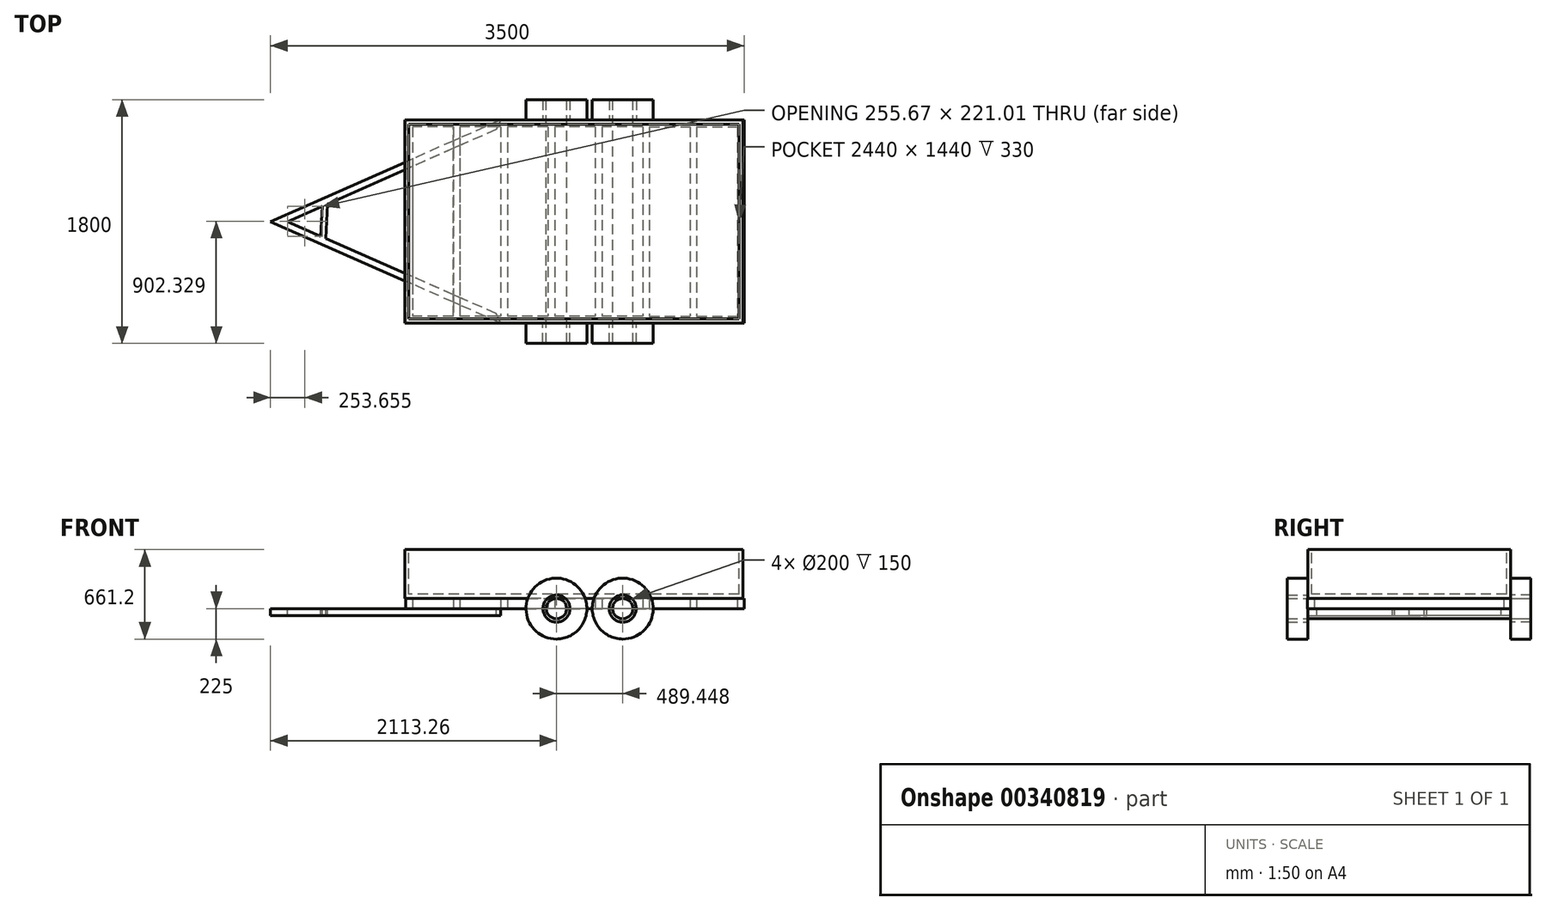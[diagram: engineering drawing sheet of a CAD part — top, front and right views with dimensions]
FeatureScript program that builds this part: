
annotation { "Feature Type Name" : "Feature", "Feature Type Description" : "" }
export const myFeature = defineFeature(function(context is Context, id is Id, definition is map)
    precondition{}
    {
        {
            var Q0;
            Q0=qCreatedBy(makeId("Top.planeOp"),FACE);
            var sketch = newSketch(context, id + "F0", { "sketchPlane" : qUnion([Q0])});
            skLineSegment(sketch, "E0.bottom", {"start": v(1069.78, 749.77) * mm, "end": v(-1430.22, 749.77) * mm});
            skLineSegment(sketch, "E0.top", {"start": v(1069.78, -750.23) * mm, "end": v(-1430.22, -750.23) * mm});
            skLineSegment(sketch, "E0.left", {"start": v(1069.78, 749.77) * mm, "end": v(1069.78, -750.23) * mm});
            skLineSegment(sketch, "E0.right", {"start": v(-1430.22, 749.77) * mm, "end": v(-1430.22, -750.23) * mm});
            skLineSegment(sketch, "E1.0", {"start": v(-1380.22, 699.77) * mm, "end": v(-1380.22, -700.23) * mm});
            skLineSegment(sketch, "E2.left", {"start": v(-1080.22, 699.77) * mm, "end": v(-1080.22, -700.23) * mm});
            skLineSegment(sketch, "E3.trimOffspring", {"start": v(-1080.22, 699.77) * mm, "end": v(-1380.22, 699.77) * mm});
            skLineSegment(sketch, "E4.trimOffspring", {"start": v(-1080.22, -700.23) * mm, "end": v(-1380.22, -700.23) * mm});
            skLineSegment(sketch, "E5.1.0.0", {"start": v(-730.22, 699.77) * mm, "end": v(-730.22, -700.23) * mm});
            skLineSegment(sketch, "E5.1.0.1", {"start": v(-730.22, 699.77) * mm, "end": v(-1030.22, 699.77) * mm});
            skLineSegment(sketch, "E5.1.0.2", {"start": v(-1030.22, 699.77) * mm, "end": v(-1030.22, -700.23) * mm});
            skLineSegment(sketch, "E5.1.0.3", {"start": v(-730.22, -700.23) * mm, "end": v(-1030.22, -700.23) * mm});
            skLineSegment(sketch, "E5.2.0.0", {"start": v(-380.22, 699.77) * mm, "end": v(-380.22, -700.23) * mm});
            skLineSegment(sketch, "E5.2.0.1", {"start": v(-380.22, 699.77) * mm, "end": v(-680.22, 699.77) * mm});
            skLineSegment(sketch, "E5.2.0.2", {"start": v(-680.22, 699.77) * mm, "end": v(-680.22, -700.23) * mm});
            skLineSegment(sketch, "E5.2.0.3", {"start": v(-380.22, -700.23) * mm, "end": v(-680.22, -700.23) * mm});
            skLineSegment(sketch, "E5.3.0.0", {"start": v(-30.22, 699.77) * mm, "end": v(-30.22, -700.23) * mm});
            skLineSegment(sketch, "E5.3.0.1", {"start": v(-30.22, 699.77) * mm, "end": v(-330.22, 699.77) * mm});
            skLineSegment(sketch, "E5.3.0.2", {"start": v(-330.22, 699.77) * mm, "end": v(-330.22, -700.23) * mm});
            skLineSegment(sketch, "E5.3.0.3", {"start": v(-30.22, -700.23) * mm, "end": v(-330.22, -700.23) * mm});
            skLineSegment(sketch, "E5.4.0.0", {"start": v(319.78, 699.77) * mm, "end": v(319.78, -700.23) * mm});
            skLineSegment(sketch, "E5.4.0.1", {"start": v(319.78, 699.77) * mm, "end": v(19.78, 699.77) * mm});
            skLineSegment(sketch, "E5.4.0.2", {"start": v(19.78, 699.77) * mm, "end": v(19.78, -700.23) * mm});
            skLineSegment(sketch, "E5.4.0.3", {"start": v(319.78, -700.23) * mm, "end": v(19.78, -700.23) * mm});
            skLineSegment(sketch, "E5.direction1", {"start": v(-1080.22, -700.23) * mm, "end": v(-730.22, -700.23) * mm, "construction": true});
            skLineSegment(sketch, "E6.bottom", {"start": v(369.78, 699.77) * mm, "end": v(669.78, 699.77) * mm});
            skLineSegment(sketch, "E6.top", {"start": v(369.78, -700.23) * mm, "end": v(669.78, -700.23) * mm});
            skLineSegment(sketch, "E6.left", {"start": v(369.78, 699.77) * mm, "end": v(369.78, -700.23) * mm});
            skLineSegment(sketch, "E6.right", {"start": v(669.78, 699.77) * mm, "end": v(669.78, -700.23) * mm});
            skLineSegment(sketch, "E7.bottom", {"start": v(719.78, 699.77) * mm, "end": v(1019.78, 699.77) * mm});
            skLineSegment(sketch, "E7.top", {"start": v(719.78, -700.23) * mm, "end": v(1019.78, -700.23) * mm});
            skLineSegment(sketch, "E7.left", {"start": v(719.78, 699.77) * mm, "end": v(719.78, -700.23) * mm});
            skLineSegment(sketch, "E7.right", {"start": v(1019.78, 699.77) * mm, "end": v(1019.78, -700.23) * mm});
            skSolve(sketch);
        }
        {
            var Q0;
            Q0 = qSketchRegion(id + "F0", true);
            var Q1;
            Q1 = qSketchRegion(id + "F2", true);
            extrude(context, id + "F1", {"entities" : qUnion([Q0, Q1]), "depth" : 76.2 * mm});
        }
        {
            var Q0;
            Q0=makeQuery(id+"F1.opExtrude","CAP_FACE",FACE,{"disambiguationData":[OSD([sQuery(id+"F0.wireOp",EDGE,"E0.bottom"),sQuery(id+"F0.wireOp",EDGE,"E0.top"),sQuery(id+"F0.wireOp",EDGE,"E0.left"),sQuery(id+"F0.wireOp",EDGE,"E0.right"),sQuery(id+"F0.wireOp",EDGE,"E1.0"),sQuery(id+"F0.wireOp",EDGE,"E2.left"),sQuery(id+"F0.wireOp",EDGE,"E3.trimOffspring"),sQuery(id+"F0.wireOp",EDGE,"E4.trimOffspring"),sQuery(id+"F0.wireOp",EDGE,"E5.1.0.0"),sQuery(id+"F0.wireOp",EDGE,"E5.1.0.1"),sQuery(id+"F0.wireOp",EDGE,"E5.1.0.2"),sQuery(id+"F0.wireOp",EDGE,"E5.1.0.3"),sQuery(id+"F0.wireOp",EDGE,"E5.2.0.0"),sQuery(id+"F0.wireOp",EDGE,"E5.2.0.1"),sQuery(id+"F0.wireOp",EDGE,"E5.2.0.2"),sQuery(id+"F0.wireOp",EDGE,"E5.2.0.3"),sQuery(id+"F0.wireOp",EDGE,"E5.3.0.0"),sQuery(id+"F0.wireOp",EDGE,"E5.3.0.1"),sQuery(id+"F0.wireOp",EDGE,"E5.3.0.2"),sQuery(id+"F0.wireOp",EDGE,"E5.3.0.3"),sQuery(id+"F0.wireOp",EDGE,"E5.4.0.0"),sQuery(id+"F0.wireOp",EDGE,"E5.4.0.1"),sQuery(id+"F0.wireOp",EDGE,"E5.4.0.2"),sQuery(id+"F0.wireOp",EDGE,"E5.4.0.3")])],"isStart":true});
            var sketch = newSketch(context, id + "F2", { "sketchPlane" : qUnion([Q0])});
            skLineSegment(sketch, "E8", {"start": v(-730.22, 750.23) * mm, "end": v(-2430.22, 0) * mm});
            skLineSegment(sketch, "E9.0", {"start": v(-761.7, 680.81) * mm, "end": v(-2021.93, 124.66) * mm});
            skLineSegment(sketch, "E10", {"start": v(-730.22, 750.23) * mm, "end": v(-761.7, 680.81) * mm});
            skLineSegment(sketch, "E11", {"start": v(1069.78, 0) * mm, "end": v(-2619.5, 0) * mm, "construction": true});
            skLineSegment(sketch, "E12.0.MirrorCS", {"start": v(-730.22, -750.23) * mm, "end": v(-761.7, -680.81) * mm});
            skLineSegment(sketch, "E12.1.MirrorCS", {"start": v(-761.7, -680.81) * mm, "end": v(-2009.76, -130.03) * mm});
            skLineSegment(sketch, "E12.2.MirrorCS", {"start": v(-730.22, -750.23) * mm, "end": v(-2430.22, 0) * mm});
            skPoint(sketch, "E13.orphan", {"position": v(-2224.3, -35.35) * mm});
            skPoint(sketch, "E14.orphan", {"position": v(-2224.3, 35.35) * mm});
            skLineSegment(sketch, "E15.left", {"start": v(-2059.28, 108.17) * mm, "end": v(-2048.73, -112.83) * mm});
            skLineSegment(sketch, "E15.right", {"start": v(-2021.93, 124.66) * mm, "end": v(-2009.76, -130.03) * mm});
            skLineSegment(sketch, "E16.trimOffspring", {"start": v(-2048.73, -112.83) * mm, "end": v(-2304.4, 0) * mm});
            skLineSegment(sketch, "E17.trimOffspring", {"start": v(-2059.28, 108.17) * mm, "end": v(-2304.4, 0) * mm});
            skSolve(sketch);
        }
        {
            var Q0;
            Q0=qSketchRegion(id+"F2",true);
            extrude(context, id + "F3", {"entities" : qUnion([Q0]), "operationType" : NewBodyOperationType.ADD, "depth" : 50.8 * mm});
        }
        {
            var Q0;
            Q0=qCreatedBy(makeId("Front.planeOp"),FACE);
            var sketch = newSketch(context, id + "F4", { "sketchPlane" : qUnion([Q0])});
            skLineSegment(sketch, "E18.bottom", {"start": v(-1437.5, 76.2) * mm, "end": v(1062.5, 76.2) * mm});
            skLineSegment(sketch, "E18.top", {"start": v(-1437.5, 436.2) * mm, "end": v(1062.5, 436.2) * mm});
            skLineSegment(sketch, "E18.left", {"start": v(-1437.5, 76.2) * mm, "end": v(-1437.5, 436.2) * mm});
            skLineSegment(sketch, "E18.right", {"start": v(1062.5, 76.2) * mm, "end": v(1062.5, 436.2) * mm});
            skSolve(sketch);
        }
        {
            var Q0;
            Q0=makeQuery(id+"F4.imprint","IMPRINT",FACE,{"disambiguationData":[TD([[makeQuery(id+"F4.imprint","IMPRINT",EDGE,{"derivedFrom":sQuery(id+"F4.wireOp",EDGE,"E18.bottom")}),1.0]])]});
            extrude(context, id + "F5", {"entities" : qUnion([Q0]), "operationType" : NewBodyOperationType.ADD, "endBound" : BoundingType.SYMMETRIC, "oppositeDirection" : true, "depth" : 1500 * mm});
        }
        {
            var Q0;
            Q0=makeQuery(id+"F5.opExtrude","SWEPT_FACE",FACE,{"disambiguationData":[OSD([sQuery(id+"F4.wireOp",EDGE,"E18.top")])]});
            shell(context, id + "F6", {"entities" : qUnion([Q0]), "thickness" : 30 * mm});
        }
        {
            var Q0;
            Q0=qCreatedBy(makeId("Front.planeOp"),FACE);
            var sketch = newSketch(context, id + "F7", { "sketchPlane" : qUnion([Q0])});
            skCircle(sketch, "E19", {"center": v(-316.97, 0) * mm, "radius": 225 * mm});
            skCircle(sketch, "E20", {"center": v(172.48, 0) * mm, "radius": 225 * mm});
            skCircle(sketch, "E21", {"center": v(-316.97, 0) * mm, "radius": 100 * mm});
            skCircle(sketch, "E22", {"center": v(172.48, 0) * mm, "radius": 100 * mm});
            skSolve(sketch);
        }
        {
            var Q0;
            Q0=makeQuery(id+"F7.imprint","IMPRINT",FACE,{"disambiguationData":[TD([[makeQuery(id+"F7.imprint","IMPRINT",EDGE,{"derivedFrom":sQuery(id+"F7.wireOp",EDGE,"E19")}),1.0]])]});
            var Q1;
            Q1=makeQuery(id+"F7.imprint","IMPRINT",FACE,{"disambiguationData":[TD([[makeQuery(id+"F7.imprint","IMPRINT",EDGE,{"derivedFrom":sQuery(id+"F7.wireOp",EDGE,"E20")}),1.0]])]});
            extrude(context, id + "F8", {"entities" : qUnion([Q0, Q1]), "operationType" : NewBodyOperationType.ADD, "oppositeDirection" : true, "offsetDistance" : 25 * mm, "depth" : 900 * mm, "hasSecondDirection" : true, "secondDirectionOppositeDirection" : true, "secondDirectionDepth" : 750 * mm});
        }
        {
            var Q0;
            Q0 = qSketchRegion(id + "F7", true);
            extrude(context, id + "F9", {"entities" : qUnion([Q0]), "operationType" : NewBodyOperationType.ADD, "offsetDistance" : 25 * mm, "depth" : 900 * mm, "hasSecondDirection" : true, "secondDirectionOppositeDirection" : false, "secondDirectionDepth" : 750 * mm});
        }
        {
            var Q0;
            Q0=qCreatedBy(makeId("Front.planeOp"),FACE);
            var sketch = newSketch(context, id + "F10", { "sketchPlane" : qUnion([Q0])});
            skCircle(sketch, "E23", {"center": v(-316.97, 0) * mm, "radius": 75 * mm});
            skCircle(sketch, "E24", {"center": v(172.48, 0) * mm, "radius": 75 * mm});
            skSolve(sketch);
        }
        {
            var Q0;
            Q0 = qSketchRegion(id + "F10", true);
            extrude(context, id + "F11", {"entities" : qUnion([Q0]), "offsetDistance" : 25 * mm, "depth" : 900 * mm, "hasSecondDirection" : true, "secondDirectionOppositeDirection" : true, "secondDirectionDepth" : 900 * mm});
        }
    });
